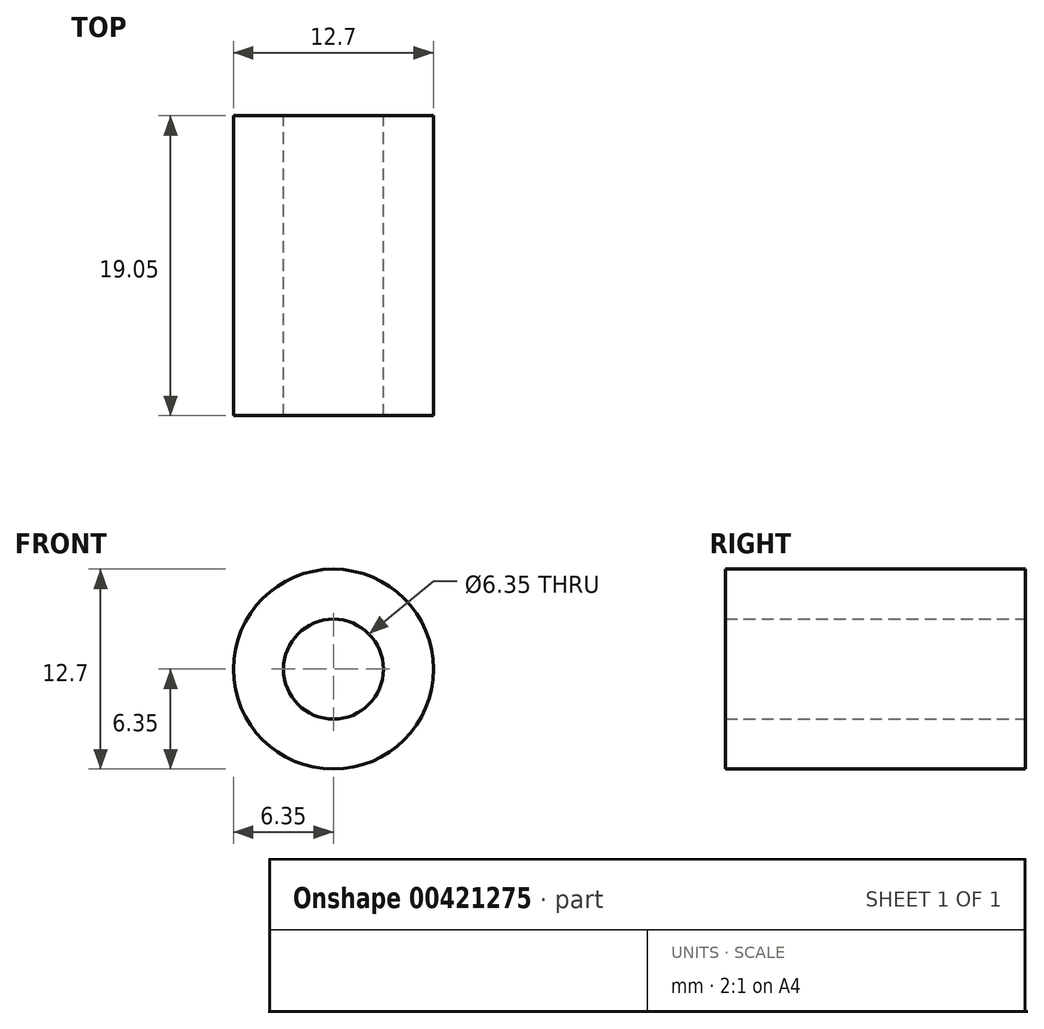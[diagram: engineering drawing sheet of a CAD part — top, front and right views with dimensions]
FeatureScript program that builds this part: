
annotation { "Feature Type Name" : "Feature", "Feature Type Description" : "" }
export const myFeature = defineFeature(function(context is Context, id is Id, definition is map)
    precondition{}
    {
        {
            var Q0;
            Q0=qCreatedBy(makeId("Front.planeOp"),FACE);
            var sketch = newSketch(context, id + "F0", { "sketchPlane" : qUnion([Q0])});
            skCircle(sketch, "E0", {"center": v(0, 0) * mm, "radius": 3.18 * mm});
            skCircle(sketch, "E1", {"center": v(0, 0) * mm, "radius": 6.35 * mm});
            skSolve(sketch);
        }
        {
            var Q0;
            Q0 = qSketchRegion(id + "F0", true);
            extrude(context, id + "F1", {"entities" : qUnion([Q0]), "depth" : 19.05 * mm, "offsetDistance" : 25.4 * mm});
        }
    });
